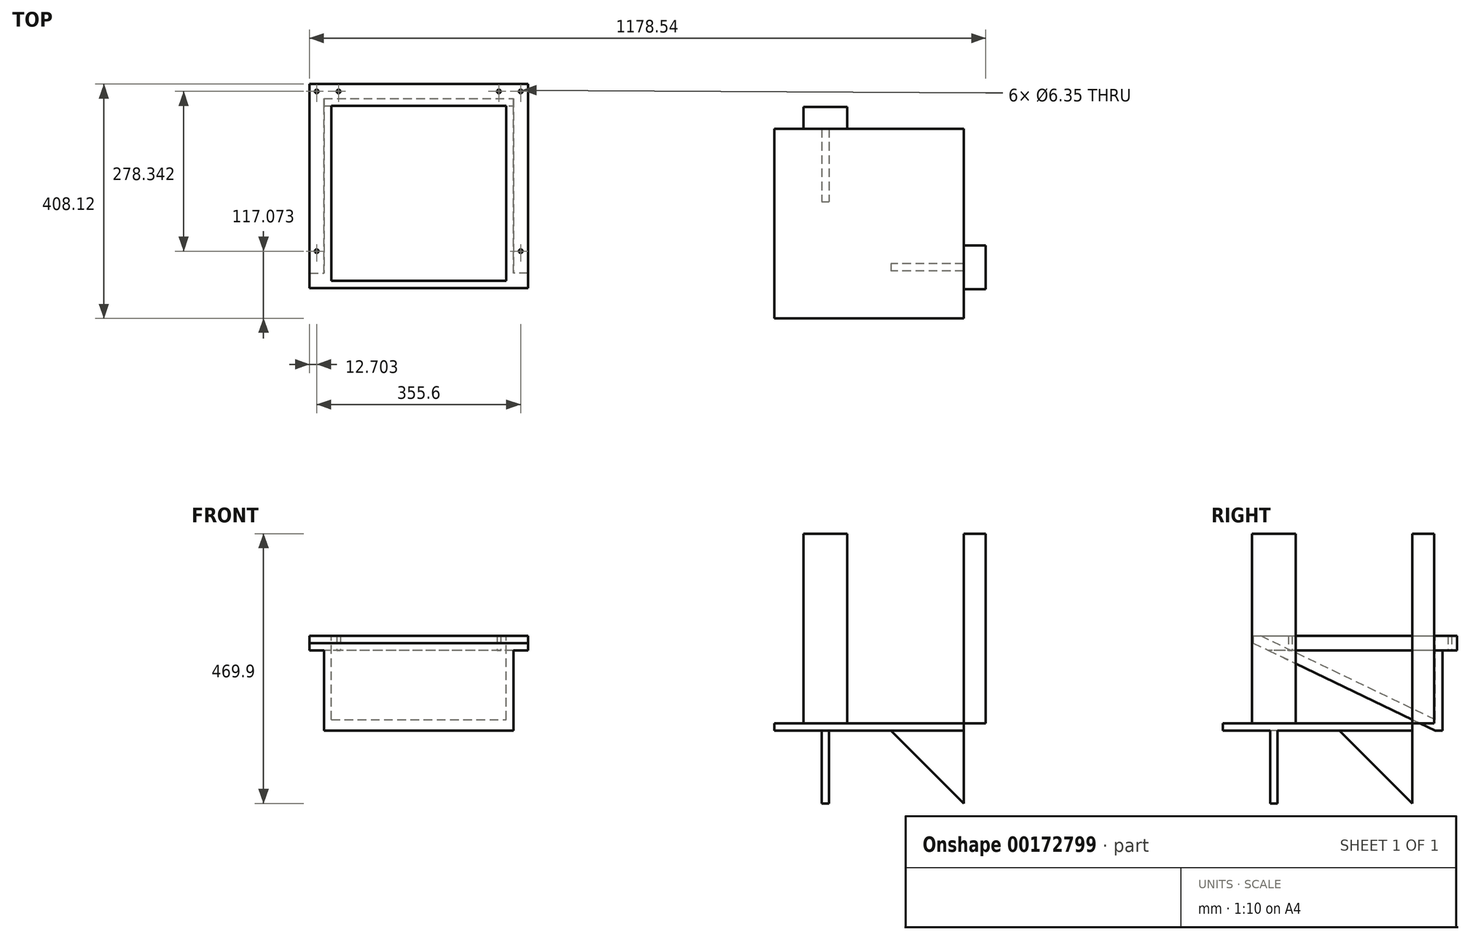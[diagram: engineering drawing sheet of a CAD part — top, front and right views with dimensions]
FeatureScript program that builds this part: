
annotation { "Feature Type Name" : "Feature", "Feature Type Description" : "" }
export const myFeature = defineFeature(function(context is Context, id is Id, definition is map)
    precondition{}
    {
        {
            var Q0;
            Q0=qCreatedBy(makeId("Top.planeOp"),FACE);
            var sketch = newSketch(context, id + "F0", { "sketchPlane" : qUnion([Q0])});
            skLineSegment(sketch, "E0.bottom", {"start": v(-171.25, 246.68) * mm, "end": v(158.95, 246.68) * mm});
            skLineSegment(sketch, "E0.top", {"start": v(-171.25, -83.52) * mm, "end": v(158.95, -83.52) * mm});
            skLineSegment(sketch, "E0.left", {"start": v(-171.25, 246.68) * mm, "end": v(-171.25, -83.52) * mm});
            skLineSegment(sketch, "E0.right", {"start": v(158.95, 246.68) * mm, "end": v(158.95, -83.52) * mm});
            skSolve(sketch);
        }
        {
            var Q0;
            Q0=makeQuery(id+"F0.imprint","IMPRINT",FACE,{"disambiguationData":[TD([[makeQuery(id+"F0.imprint","IMPRINT",EDGE,{"derivedFrom":sQuery(id+"F0.wireOp",EDGE,"E0.bottom")}),-1.0]])]});
            extrude(context, id + "F1", {"entities" : qUnion([Q0]), "depth" : 165.1 * mm});
        }
        {
            var Q0;
            Q0=makeQuery(id+"F1.opExtrude","CAP_FACE",FACE,{"disambiguationData":[OSD([sQuery(id+"F0.wireOp",EDGE,"E0.bottom"),sQuery(id+"F0.wireOp",EDGE,"E0.top"),sQuery(id+"F0.wireOp",EDGE,"E0.left"),sQuery(id+"F0.wireOp",EDGE,"E0.right")])],"isStart":false});
            var sketch = newSketch(context, id + "F2", { "sketchPlane" : qUnion([Q0])});
            skLineSegment(sketch, "E1.bottom", {"start": v(-158.55, 233.98) * mm, "end": v(146.25, 233.98) * mm});
            skLineSegment(sketch, "E1.top", {"start": v(-158.55, -70.82) * mm, "end": v(146.25, -70.82) * mm});
            skLineSegment(sketch, "E1.left", {"start": v(-158.55, 233.98) * mm, "end": v(-158.55, -70.82) * mm});
            skLineSegment(sketch, "E1.right", {"start": v(146.25, 233.98) * mm, "end": v(146.25, -70.82) * mm});
            skSolve(sketch);
        }
        {
            var Q0;
            Q0=makeQuery(id+"F2.imprint","IMPRINT",FACE,{"disambiguationData":[TD([[makeQuery(id+"F2.imprint","IMPRINT",EDGE,{"derivedFrom":sQuery(id+"F2.wireOp",EDGE,"E1.bottom")}),-1.0]])]});
            extrude(context, id + "F3", {"entities" : qUnion([Q0]), "operationType" : NewBodyOperationType.REMOVE, "oppositeDirection" : true, "depth" : 152.4 * mm});
        }
        {
            var Q0;
            Q0=makeQuery(id+"F1.opExtrude","SWEPT_FACE",FACE,{"disambiguationData":[OSD([sQuery(id+"F0.wireOp",EDGE,"E0.top")])]});
            var sketch = newSketch(context, id + "F4", { "sketchPlane" : qUnion([Q0])});
            skLineSegment(sketch, "E2", {"start": v(-171.25, 152.4) * mm, "end": v(146.25, 0) * mm});
            skSolve(sketch);
        }
        {
            var Q0;
            {var subQ0=sQuery(id+"F4.wireOp",EDGE,"E2");Q0=makeQuery(id+"F4.imprint","IMPRINT",FACE,{"disambiguationData":[TD([[makeQuery(id+"F4.imprint","IMPRINT",EDGE,{"derivedFrom":subQ0}),-1.0]])]});}
            extrude(context, id + "F5", {"entities" : qUnion([Q0]), "operationType" : NewBodyOperationType.REMOVE, "oppositeDirection" : true, "depth" : 330.2 * mm});
        }
        {
            var Q0;
            Q0=makeQuery(id+"F3.boolean.opBoolean","COPY",FACE,{"derivedFrom":makeQuery(id+"F3.opExtrude","SWEPT_FACE",FACE,{"disambiguationData":[OSD([sQuery(id+"F2.wireOp",EDGE,"E1.top")])]})});
            var sketch = newSketch(context, id + "F6", { "sketchPlane" : qUnion([Q0])});
            skLineSegment(sketch, "E3", {"start": v(-158.95, 12.7) * mm, "end": v(158.55, 165.1) * mm});
            skSolve(sketch);
        }
        {
            var Q0;
            {var subQ0=sQuery(id+"F2.wireOp",EDGE,"E1.top");var subQ1=makeQuery(id+"F3.boolean.opBoolean","COPY",EDGE,{"derivedFrom":makeQuery(id+"F3.opExtrude","CAP_EDGE",EDGE,{"disambiguationData":[OSD([subQ0])],"isStart":false})});Q0=makeQuery(id+"F6.imprint","IMPRINT",FACE,{"disambiguationData":[TD([[makeQuery(id+"F6.imprint","IMPRINT",EDGE,{"derivedFrom":subQ1}),-1.0]])]});}
            extrude(context, id + "F7", {"entities" : qUnion([Q0]), "operationType" : NewBodyOperationType.ADD, "depth" : 304.8 * mm});
        }
        {
            var Q0;
            Q0=makeQuery(id+"F1.opExtrude","SWEPT_FACE",FACE,{"disambiguationData":[OSD([sQuery(id+"F0.wireOp",EDGE,"E0.right")])]});
            var sketch = newSketch(context, id + "F8", { "sketchPlane" : qUnion([Q0])});
            skLineSegment(sketch, "E4", {"start": v(-83.52, 139.7) * mm, "end": v(246.68, 139.7) * mm});
            skSolve(sketch);
        }
        {
            var Q0;
            {var subQ0=sQuery(id+"F8.wireOp",EDGE,"E4");Q0=makeQuery(id+"F8.imprint","IMPRINT",FACE,{"disambiguationData":[TD([[makeQuery(id+"F8.imprint","IMPRINT",EDGE,{"derivedFrom":subQ0}),1.0]])]});}
            extrude(context, id + "F9", {"entities" : qUnion([Q0]), "operationType" : NewBodyOperationType.ADD, "depth" : 25.4 * mm});
        }
        {
            var Q0;
            {var subQ0=sQuery(id+"F0.wireOp",EDGE,"E0.bottom");Q0=makeQuery(id+"F9.boolean.opBoolean","MERGE",FACE,{"derivedFrom":[makeQuery(id+"F1.opExtrude","SWEPT_FACE",FACE,{"disambiguationData":[OSD([subQ0])]}),makeQuery(id+"F9.opExtrude","SWEPT_FACE",FACE,{"disambiguationData":[OSD([subQ0,sQuery(id+"F0.wireOp",EDGE,"E0.right")])]})]});}
            var sketch = newSketch(context, id + "F10", { "sketchPlane" : qUnion([Q0])});
            skLineSegment(sketch, "E5", {"start": v(-158.95, 139.7) * mm, "end": v(144.79, 139.7) * mm});
            skSolve(sketch);
        }
        {
            var Q0;
            {var subQ3=sQuery(id+"F10.wireOp",EDGE,"E5");Q0=makeQuery(id+"F10.imprint","IMPRINT",FACE,{"disambiguationData":[TD([[makeQuery(id+"F10.imprint","IMPRINT",EDGE,{"derivedFrom":subQ3}),1.0]])]});}
            extrude(context, id + "F11", {"entities" : qUnion([Q0]), "operationType" : NewBodyOperationType.ADD, "depth" : 25.4 * mm});
        }
        {
            var Q0;
            {var subQ0=sQuery(id+"F0.wireOp",EDGE,"E0.top");Q0=makeQuery(id+"F9.boolean.opBoolean","MERGE",FACE,{"derivedFrom":[makeQuery(id+"F1.opExtrude","SWEPT_FACE",FACE,{"disambiguationData":[OSD([subQ0])]}),makeQuery(id+"F9.opExtrude","SWEPT_FACE",FACE,{"disambiguationData":[OSD([subQ0,sQuery(id+"F0.wireOp",EDGE,"E0.right")])]})]});}
            var sketch = newSketch(context, id + "F12", { "sketchPlane" : qUnion([Q0])});
            skLineSegment(sketch, "E6", {"start": v(163.49, 139.7) * mm, "end": v(-144.79, 139.7) * mm});
            skSolve(sketch);
        }
        {
            var Q0;
            {var subQ0=sQuery(id+"F0.wireOp",EDGE,"E0.top");var subQ1=makeQuery(id+"F1.opExtrude","SWEPT_EDGE",EDGE,{"disambiguationData":[OSD([subQ0,sQuery(id+"F0.wireOp",EDGE,"E0.left")])]});Q0=makeQuery(id+"F12.imprint","IMPRINT",FACE,{"disambiguationData":[TD([[makeQuery(id+"F12.imprint","IMPRINT",EDGE,{"derivedFrom":subQ1}),1.0]])]});}
            extrude(context, id + "F13", {"entities" : qUnion([Q0]), "operationType" : NewBodyOperationType.ADD, "depth" : 25.4 * mm});
        }
        {
            var Q0;
            {var subQ0=sQuery(id+"F8.wireOp",EDGE,"E4");Q0=makeQuery(id+"F13.boolean.opBoolean","MERGE",FACE,{"derivedFrom":[makeQuery(id+"F11.boolean.opBoolean","MERGE",FACE,{"derivedFrom":[makeQuery(id+"F9.opExtrude","SWEPT_FACE",FACE,{"disambiguationData":[OSD([subQ0])]}),makeQuery(id+"F11.opExtrude","SWEPT_FACE",FACE,{"disambiguationData":[OSD([sQuery(id+"F0.wireOp",EDGE,"E0.bottom"),sQuery(id+"F0.wireOp",EDGE,"E0.right"),subQ0,sQuery(id+"F10.wireOp",EDGE,"E5")])]})]}),makeQuery(id+"F13.opExtrude","SWEPT_FACE",FACE,{"disambiguationData":[OSD([sQuery(id+"F12.wireOp",EDGE,"E6")])]})]});}
            var sketch = newSketch(context, id + "F14", { "sketchPlane" : qUnion([Q0])});
            skCircle(sketch, "E7", {"center": v(171.65, 96.22) * mm, "radius": 3.18 * mm});
            skCircle(sketch, "E8", {"center": v(171.65, -259.38) * mm, "radius": 3.18 * mm});
            skCircle(sketch, "E9", {"center": v(-106.69, -259.38) * mm, "radius": 3.18 * mm});
            skCircle(sketch, "E10", {"center": v(-106.69, 96.22) * mm, "radius": 3.18 * mm});
            skCircle(sketch, "E11", {"center": v(171.65, 58.12) * mm, "radius": 3.18 * mm});
            skCircle(sketch, "E12", {"center": v(171.65, -221.28) * mm, "radius": 3.18 * mm});
            skSolve(sketch);
        }
        {
            var Q0;
            Q0=makeQuery(id+"F14.imprint","IMPRINT",FACE,{"disambiguationData":[TD([[makeQuery(id+"F14.imprint","IMPRINT",EDGE,{"derivedFrom":sQuery(id+"F14.wireOp",EDGE,"E12")}),1.0]])]});
            extrude(context, id + "F15", {"entities" : qUnion([Q0]), "operationType" : NewBodyOperationType.REMOVE, "oppositeDirection" : true, "depth" : 25.4 * mm});
        }
        {
            var Q0;
            Q0=makeQuery(id+"F14.imprint","IMPRINT",FACE,{"disambiguationData":[TD([[makeQuery(id+"F14.imprint","IMPRINT",EDGE,{"derivedFrom":sQuery(id+"F14.wireOp",EDGE,"E8")}),1.0]])]});
            extrude(context, id + "F16", {"entities" : qUnion([Q0]), "operationType" : NewBodyOperationType.REMOVE, "oppositeDirection" : true, "depth" : 25.4 * mm});
        }
        {
            var Q0;
            Q0=makeQuery(id+"F14.imprint","IMPRINT",FACE,{"disambiguationData":[TD([[makeQuery(id+"F14.imprint","IMPRINT",EDGE,{"derivedFrom":sQuery(id+"F14.wireOp",EDGE,"E9")}),1.0]])]});
            extrude(context, id + "F17", {"entities" : qUnion([Q0]), "operationType" : NewBodyOperationType.REMOVE, "oppositeDirection" : true, "depth" : 25.4 * mm});
        }
        {
            var Q0;
            Q0=makeQuery(id+"F14.imprint","IMPRINT",FACE,{"disambiguationData":[TD([[makeQuery(id+"F14.imprint","IMPRINT",EDGE,{"derivedFrom":sQuery(id+"F14.wireOp",EDGE,"E7")}),1.0]])]});
            var Q1;
            Q1=makeQuery(id+"F14.imprint","IMPRINT",FACE,{"disambiguationData":[TD([[makeQuery(id+"F14.imprint","IMPRINT",EDGE,{"derivedFrom":sQuery(id+"F14.wireOp",EDGE,"E11")}),1.0]])]});
            var Q2;
            Q2=makeQuery(id+"F14.imprint","IMPRINT",FACE,{"disambiguationData":[TD([[makeQuery(id+"F14.imprint","IMPRINT",EDGE,{"derivedFrom":sQuery(id+"F14.wireOp",EDGE,"E10")}),1.0]])]});
            extrude(context, id + "F18", {"entities" : qUnion([Q0, Q1, Q2]), "operationType" : NewBodyOperationType.REMOVE, "oppositeDirection" : true, "depth" : 25.4 * mm});
        }
        {
            var Q0;
            Q0=makeQuery(id+"F1.opExtrude","SWEPT_BODY",BODY,{"disambiguationData":[OSD([sQuery(id+"F0.wireOp",EDGE,"E0.bottom"),sQuery(id+"F0.wireOp",EDGE,"E0.top"),sQuery(id+"F0.wireOp",EDGE,"E0.left"),sQuery(id+"F0.wireOp",EDGE,"E0.right")])]});
            var Q1;
            {var subQ0=sQuery(id+"F0.wireOp",EDGE,"E0.right");var subQ1=sQuery(id+"F0.wireOp",EDGE,"E0.top");Q1=makeQuery(id+"F13.opExtrude","CAP_EDGE",EDGE,{"disambiguationData":[OSD([subQ1,subQ0]),TDD([makeQuery(id+"F12.imprint","IMPRINT",EDGE,{"derivedFrom":makeQuery(id+"F9.opExtrude","CAP_EDGE",EDGE,{"disambiguationData":[OSD([subQ1,subQ0])],"isStart":false})})])],"isStart":false});}
            transform(context, id + "F19", {"entities" : qUnion([Q0]), "transformType" : TransformType.ROTATION, "transformAxis" : qUnion([Q1]), "angle" : 90 * degree, "oppositeDirection" : true, "makeCopy" : false});
        }
        {
            var Q0;
            Q0=qCreatedBy(makeId("Top.planeOp"),FACE);
            var sketch = newSketch(context, id + "F20", { "sketchPlane" : qUnion([Q0])});
            skLineSegment(sketch, "E13.bottom", {"start": v(613.6, -186.84) * mm, "end": v(943.8, -186.84) * mm});
            skLineSegment(sketch, "E13.top", {"start": v(613.6, -517.04) * mm, "end": v(943.8, -517.04) * mm});
            skLineSegment(sketch, "E13.left", {"start": v(613.6, -186.84) * mm, "end": v(613.6, -517.04) * mm});
            skLineSegment(sketch, "E13.right", {"start": v(943.8, -186.84) * mm, "end": v(943.8, -517.04) * mm});
            skLineSegment(sketch, "E14.bottom", {"start": v(613.6, -186.84) * mm, "end": v(689.8, -186.84) * mm});
            skLineSegment(sketch, "E14.top", {"start": v(613.6, -148.74) * mm, "end": v(689.8, -148.74) * mm});
            skLineSegment(sketch, "E14.left", {"start": v(613.6, -186.84) * mm, "end": v(613.6, -148.74) * mm});
            skLineSegment(sketch, "E14.right", {"start": v(689.8, -186.84) * mm, "end": v(689.8, -148.74) * mm});
            skLineSegment(sketch, "E15.bottom", {"start": v(943.8, -517.04) * mm, "end": v(981.9, -517.04) * mm});
            skLineSegment(sketch, "E15.top", {"start": v(943.8, -440.84) * mm, "end": v(981.9, -440.84) * mm});
            skLineSegment(sketch, "E15.left", {"start": v(943.8, -517.04) * mm, "end": v(943.8, -440.84) * mm});
            skLineSegment(sketch, "E15.right", {"start": v(981.9, -517.04) * mm, "end": v(981.9, -440.84) * mm});
            skSolve(sketch);
        }
        {
            var Q0;
            Q0=makeQuery(id+"F20.imprint","IMPRINT",FACE,{"disambiguationData":[TD([[makeQuery(id+"F20.imprint","IMPRINT",EDGE,{"derivedFrom":sQuery(id+"F20.wireOp",EDGE,"E13.bottom")}),-1.0]])]});
            extrude(context, id + "F21", {"entities" : qUnion([Q0]), "depth" : 12.7 * mm});
        }
        {
            var Q0;
            Q0=makeQuery(id+"F21.opExtrude","SWEPT_FACE",FACE,{"disambiguationData":[OSD([sQuery(id+"F20.wireOp",EDGE,"E13.right"),sQuery(id+"F20.wireOp",EDGE,"E15.left")])]});
            var sketch = newSketch(context, id + "F22", { "sketchPlane" : qUnion([Q0])});
            skLineSegment(sketch, "E16.bottom", {"start": v(-466.24, 0) * mm, "end": v(-390.04, 0) * mm});
            skLineSegment(sketch, "E16.top", {"start": v(-466.24, 342.9) * mm, "end": v(-390.04, 342.9) * mm});
            skLineSegment(sketch, "E16.left", {"start": v(-466.24, 0) * mm, "end": v(-466.24, 342.9) * mm});
            skLineSegment(sketch, "E16.right", {"start": v(-390.04, 0) * mm, "end": v(-390.04, 342.9) * mm});
            skLineSegment(sketch, "E17.bottom", {"start": v(-390.04, 0) * mm, "end": v(-466.24, 0) * mm});
            skLineSegment(sketch, "E17.top", {"start": v(-390.04, 0) * mm, "end": v(-466.24, 0) * mm});
            skLineSegment(sketch, "E17.left", {"start": v(-390.04, 0) * mm, "end": v(-390.04, 0) * mm});
            skLineSegment(sketch, "E17.right", {"start": v(-466.24, 0) * mm, "end": v(-466.24, 0) * mm});
            skLineSegment(sketch, "E18.top", {"start": v(-466.24, -469.9) * mm, "end": v(-390.04, -469.9) * mm});
            skLineSegment(sketch, "E18.left", {"start": v(-466.24, 0) * mm, "end": v(-466.24, -469.9) * mm});
            skLineSegment(sketch, "E18.right", {"start": v(-390.04, 0) * mm, "end": v(-390.04, -469.9) * mm});
            skSolve(sketch);
        }
        {
            var Q0;
            {var subQ0=sQuery(id+"F22.wireOp",EDGE,"E16.top");Q0=makeQuery(id+"F22.imprint","IMPRINT",FACE,{"disambiguationData":[TD([[makeQuery(id+"F22.imprint","IMPRINT",EDGE,{"derivedFrom":subQ0}),-1.0]])]});}
            var Q1;
            {var subQ0=sQuery(id+"F22.wireOp",EDGE,"E16.bottom");Q1=makeQuery(id+"F22.imprint","IMPRINT",FACE,{"disambiguationData":[TD([[makeQuery(id+"F22.imprint","IMPRINT",EDGE,{"derivedFrom":subQ0}),1.0]])]});}
            var Q2;
            Q2=makeQuery(id+"F22.imprint","IMPRINT",FACE,{"disambiguationData":[TD([[makeQuery(id+"F22.imprint","IMPRINT",EDGE,{"derivedFrom":sQuery(id+"F22.wireOp",EDGE,"E16.bottom")}),-1.0]])]});
            extrude(context, id + "F23", {"entities" : qUnion([Q0, Q1, Q2]), "operationType" : NewBodyOperationType.ADD, "depth" : 38.1 * mm});
        }
        {
            var Q0;
            Q0=makeQuery(id+"F21.opExtrude","SWEPT_FACE",FACE,{"disambiguationData":[OSD([sQuery(id+"F20.wireOp",EDGE,"E13.bottom"),sQuery(id+"F20.wireOp",EDGE,"E14.bottom")])]});
            var sketch = newSketch(context, id + "F24", { "sketchPlane" : qUnion([Q0])});
            skLineSegment(sketch, "E19.bottom", {"start": v(-664.4, 0) * mm, "end": v(-740.6, 0) * mm});
            skLineSegment(sketch, "E19.top", {"start": v(-664.4, 342.9) * mm, "end": v(-740.6, 342.9) * mm});
            skLineSegment(sketch, "E19.left", {"start": v(-664.4, 0) * mm, "end": v(-664.4, 342.9) * mm});
            skLineSegment(sketch, "E19.right", {"start": v(-740.6, 0) * mm, "end": v(-740.6, 342.9) * mm});
            skLineSegment(sketch, "E20.top", {"start": v(-664.4, -469.9) * mm, "end": v(-740.6, -469.9) * mm});
            skLineSegment(sketch, "E20.left", {"start": v(-664.4, 0) * mm, "end": v(-664.4, -469.9) * mm});
            skLineSegment(sketch, "E20.right", {"start": v(-740.6, 0) * mm, "end": v(-740.6, -469.9) * mm});
            skSolve(sketch);
        }
        {
            var Q0;
            {var subQ0=sQuery(id+"F24.wireOp",EDGE,"E19.top");Q0=makeQuery(id+"F24.imprint","IMPRINT",FACE,{"disambiguationData":[TD([[makeQuery(id+"F24.imprint","IMPRINT",EDGE,{"derivedFrom":subQ0}),1.0]])]});}
            var Q1;
            {var subQ0=sQuery(id+"F24.wireOp",EDGE,"E19.bottom");Q1=makeQuery(id+"F24.imprint","IMPRINT",FACE,{"disambiguationData":[TD([[makeQuery(id+"F24.imprint","IMPRINT",EDGE,{"derivedFrom":subQ0}),-1.0]])]});}
            var Q2;
            Q2=makeQuery(id+"F24.imprint","IMPRINT",FACE,{"disambiguationData":[TD([[makeQuery(id+"F24.imprint","IMPRINT",EDGE,{"derivedFrom":sQuery(id+"F24.wireOp",EDGE,"E19.bottom")}),1.0]])]});
            extrude(context, id + "F25", {"entities" : qUnion([Q0, Q1, Q2]), "operationType" : NewBodyOperationType.ADD, "depth" : 38.1 * mm});
        }
        {
            var Q0;
            Q0=makeQuery(id+"F21.opExtrude","CAP_FACE",FACE,{"disambiguationData":[OSD([sQuery(id+"F20.wireOp",EDGE,"E13.bottom"),sQuery(id+"F20.wireOp",EDGE,"E13.top"),sQuery(id+"F20.wireOp",EDGE,"E13.left"),sQuery(id+"F20.wireOp",EDGE,"E13.right"),sQuery(id+"F20.wireOp",EDGE,"E14.bottom"),sQuery(id+"F20.wireOp",EDGE,"E15.left")])],"isStart":true});
            var sketch = newSketch(context, id + "F26", { "sketchPlane" : qUnion([Q0])});
            skLineSegment(sketch, "E21", {"start": v(943.8, 390.04) * mm, "end": v(943.8, 466.24) * mm});
            skLineSegment(sketch, "E22.bottom", {"start": v(696.14, 186.84) * mm, "end": v(708.84, 186.84) * mm});
            skLineSegment(sketch, "E22.top", {"start": v(696.14, 313.84) * mm, "end": v(708.84, 313.84) * mm});
            skLineSegment(sketch, "E22.left", {"start": v(696.14, 186.84) * mm, "end": v(696.14, 313.84) * mm});
            skLineSegment(sketch, "E22.right", {"start": v(708.84, 186.84) * mm, "end": v(708.84, 313.84) * mm});
            skLineSegment(sketch, "E23.bottom", {"start": v(943.8, 421.8) * mm, "end": v(816.8, 421.8) * mm});
            skLineSegment(sketch, "E23.top", {"start": v(943.8, 434.5) * mm, "end": v(816.8, 434.5) * mm});
            skLineSegment(sketch, "E23.left", {"start": v(943.8, 421.8) * mm, "end": v(943.8, 434.5) * mm});
            skLineSegment(sketch, "E23.right", {"start": v(816.8, 421.8) * mm, "end": v(816.8, 434.5) * mm});
            skSolve(sketch);
        }
        {
            var Q0;
            Q0=makeQuery(id+"F26.imprint","IMPRINT",FACE,{"disambiguationData":[TD([[makeQuery(id+"F26.imprint","IMPRINT",EDGE,{"derivedFrom":sQuery(id+"F26.wireOp",EDGE,"E22.bottom")}),1.0]])]});
            var Q1;
            Q1=makeQuery(id+"F26.imprint","IMPRINT",FACE,{"disambiguationData":[TD([[makeQuery(id+"F26.imprint","IMPRINT",EDGE,{"derivedFrom":sQuery(id+"F26.wireOp",EDGE,"E23.bottom")}),-1.0]])]});
            extrude(context, id + "F27", {"entities" : qUnion([Q0, Q1]), "operationType" : NewBodyOperationType.ADD, "depth" : 127 * mm});
        }
        {
            var Q0;
            Q0=makeQuery(id+"F27.opExtrude","SWEPT_FACE",FACE,{"disambiguationData":[OSD([sQuery(id+"F26.wireOp",EDGE,"E23.top")])]});
            var sketch = newSketch(context, id + "F28", { "sketchPlane" : qUnion([Q0])});
            skLineSegment(sketch, "E24", {"start": v(816.8, 0) * mm, "end": v(943.8, -127) * mm});
            skSolve(sketch);
        }
        {
            var Q0;
            Q0=makeQuery(id+"F27.opExtrude","SWEPT_FACE",FACE,{"disambiguationData":[OSD([sQuery(id+"F26.wireOp",EDGE,"E22.left")])]});
            var sketch = newSketch(context, id + "F29", { "sketchPlane" : qUnion([Q0])});
            skLineSegment(sketch, "E25", {"start": v(186.84, -127) * mm, "end": v(313.84, 0) * mm});
            skSolve(sketch);
        }
        {
            var Q0;
            Q0=makeQuery(id+"F28.imprint","IMPRINT",FACE,{"disambiguationData":[TD([[makeQuery(id+"F28.imprint","IMPRINT",EDGE,{"derivedFrom":sQuery(id+"F28.wireOp",EDGE,"E24")}),-1.0]])]});
            extrude(context, id + "F30", {"entities" : qUnion([Q0]), "operationType" : NewBodyOperationType.REMOVE, "oppositeDirection" : true, "depth" : 25.4 * mm});
        }
        {
            var Q0;
            Q0=makeQuery(id+"F29.imprint","IMPRINT",FACE,{"disambiguationData":[TD([[makeQuery(id+"F29.imprint","IMPRINT",EDGE,{"derivedFrom":sQuery(id+"F29.wireOp",EDGE,"E25")}),-1.0]])]});
            extrude(context, id + "F31", {"entities" : qUnion([Q0]), "operationType" : NewBodyOperationType.REMOVE, "oppositeDirection" : true, "depth" : 25.4 * mm});
        }
    });
